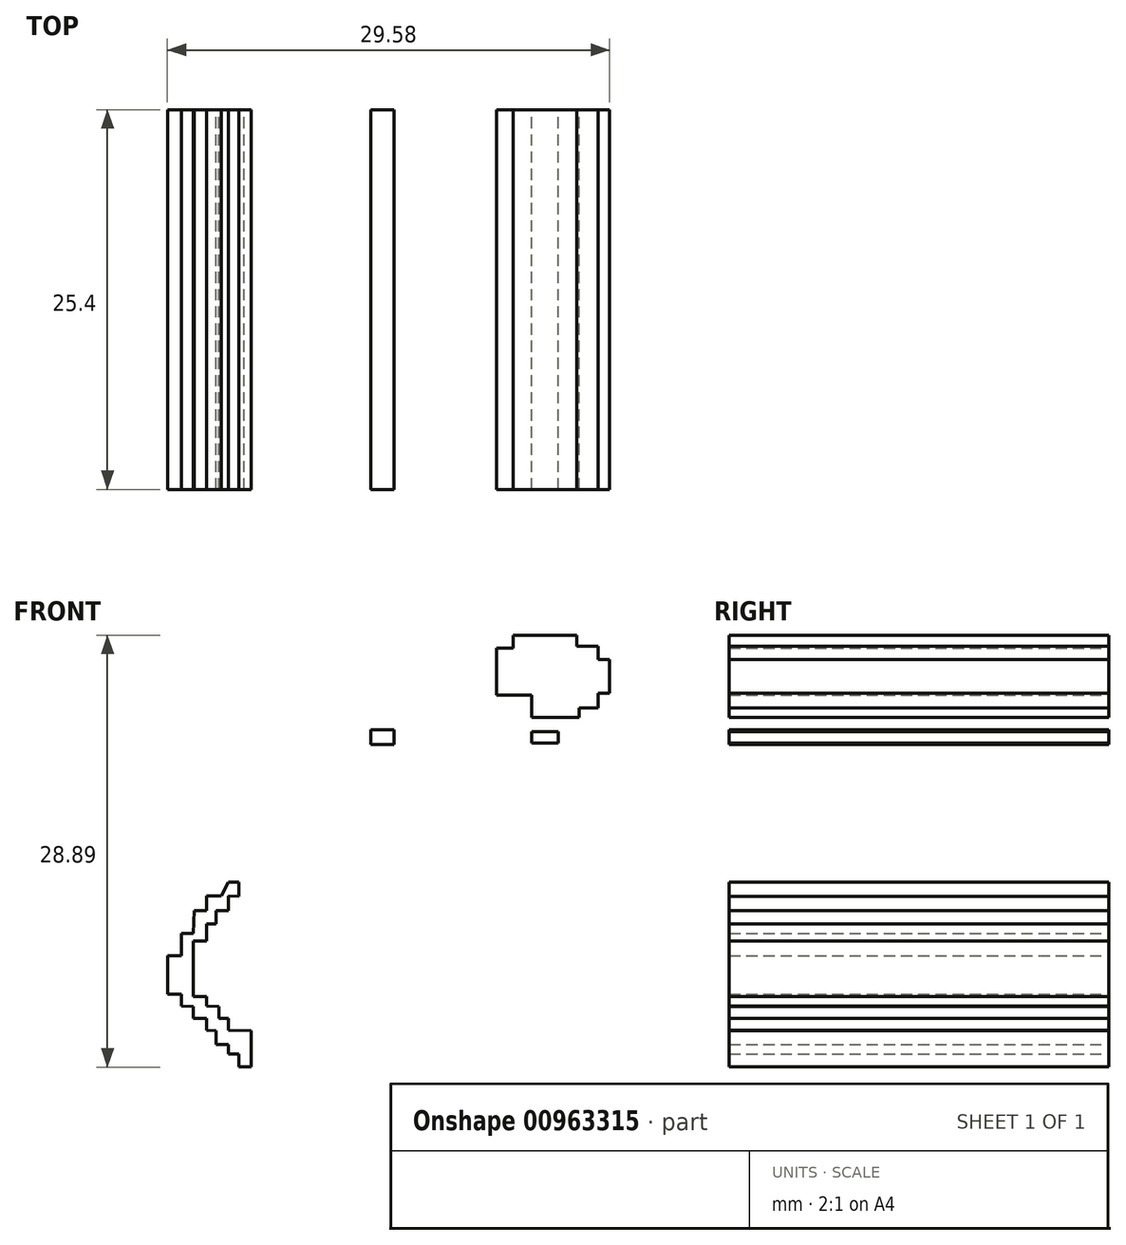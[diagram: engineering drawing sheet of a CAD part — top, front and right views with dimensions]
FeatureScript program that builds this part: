
annotation { "Feature Type Name" : "Feature", "Feature Type Description" : "" }
export const myFeature = defineFeature(function(context is Context, id is Id, definition is map)
    precondition{}
    {
        {
            var Q0;
            Q0=qCreatedBy(makeId("Front.planeOp"),FACE);
            var sketch = newSketch(context, id + "F0", { "sketchPlane" : qUnion([Q0])});
            skLineSegment(sketch, "E0", {"start": v(-16.56, -0.87) * mm, "end": v(-25.56, -0.87) * mm});
            skLineSegment(sketch, "E1", {"start": v(-25.56, -0.87) * mm, "end": v(-25.56, -1.62) * mm});
            skLineSegment(sketch, "E2", {"start": v(-25.56, -1.62) * mm, "end": v(-28.06, -1.62) * mm});
            skLineSegment(sketch, "E3", {"start": v(-28.06, -1.62) * mm, "end": v(-28.06, -2.38) * mm});
            skLineSegment(sketch, "E4", {"start": v(-28.06, -2.38) * mm, "end": v(-29.45, -2.38) * mm});
            skLineSegment(sketch, "E5", {"start": v(-29.45, -2.38) * mm, "end": v(-29.45, -3.02) * mm});
            skLineSegment(sketch, "E6", {"start": v(-29.45, -3.02) * mm, "end": v(-30.32, -3.02) * mm});
            skLineSegment(sketch, "E7", {"start": v(-30.32, -3.02) * mm, "end": v(-30.32, -4) * mm});
            skLineSegment(sketch, "E8", {"start": v(-30.32, -4) * mm, "end": v(-31.14, -4) * mm});
            skLineSegment(sketch, "E9", {"start": v(-31.14, -4) * mm, "end": v(-31.14, -4.59) * mm});
            skLineSegment(sketch, "E10", {"start": v(-31.14, -4.59) * mm, "end": v(-31.72, -4.59) * mm});
            skLineSegment(sketch, "E11", {"start": v(-31.72, -4.59) * mm, "end": v(-31.72, -5.46) * mm});
            skLineSegment(sketch, "E12", {"start": v(-31.72, -5.46) * mm, "end": v(-31.72, -6.27) * mm});
            skLineSegment(sketch, "E13", {"start": v(-31.72, -6.27) * mm, "end": v(-32.42, -6.27) * mm});
            skLineSegment(sketch, "E14", {"start": v(-32.42, -6.27) * mm, "end": v(-32.42, -11.56) * mm});
            skLineSegment(sketch, "E15", {"start": v(-32.42, -11.56) * mm, "end": v(-31.72, -11.56) * mm});
            skLineSegment(sketch, "E16", {"start": v(-31.72, -11.56) * mm, "end": v(-31.72, -13) * mm});
            skLineSegment(sketch, "E17", {"start": v(-31.72, -13) * mm, "end": v(-31.14, -13) * mm});
            skLineSegment(sketch, "E18", {"start": v(-31.14, -13) * mm, "end": v(-31.14, -14.11) * mm});
            skLineSegment(sketch, "E19", {"start": v(-31.14, -14.11) * mm, "end": v(-31.14, -14.64) * mm});
            skLineSegment(sketch, "E20", {"start": v(-31.14, -14.64) * mm, "end": v(-31.72, -14.64) * mm});
            skLineSegment(sketch, "E21", {"start": v(-31.72, -14.64) * mm, "end": v(-31.72, -15.74) * mm});
            skLineSegment(sketch, "E22", {"start": v(-31.72, -15.74) * mm, "end": v(-31.72, -17.42) * mm});
            skLineSegment(sketch, "E23", {"start": v(-31.72, -17.42) * mm, "end": v(-31.14, -17.42) * mm});
            skLineSegment(sketch, "E24", {"start": v(-31.14, -17.42) * mm, "end": v(-31.14, -18.53) * mm});
            skLineSegment(sketch, "E25", {"start": v(-31.14, -18.53) * mm, "end": v(-31.14, -19.22) * mm});
            skLineSegment(sketch, "E26", {"start": v(-31.14, -19.22) * mm, "end": v(-30.32, -19.22) * mm});
            skLineSegment(sketch, "E27", {"start": v(-30.32, -19.22) * mm, "end": v(-30.32, -19.75) * mm});
            skLineSegment(sketch, "E28", {"start": v(-30.32, -19.75) * mm, "end": v(-30.32, -20.39) * mm});
            skLineSegment(sketch, "E29", {"start": v(-30.32, -20.39) * mm, "end": v(-29.45, -20.39) * mm});
            skLineSegment(sketch, "E30", {"start": v(-29.45, -20.39) * mm, "end": v(-29.45, -20.9) * mm});
            skLineSegment(sketch, "E31", {"start": v(-29.45, -20.9) * mm, "end": v(-28.06, -20.9) * mm});
            skLineSegment(sketch, "E32", {"start": v(-28.06, -20.9) * mm, "end": v(-28.06, -21.55) * mm});
            skLineSegment(sketch, "E33", {"start": v(-28.06, -21.55) * mm, "end": v(-26.78, -21.55) * mm});
            skLineSegment(sketch, "E34", {"start": v(-26.78, -21.55) * mm, "end": v(-25.56, -21.55) * mm});
            skLineSegment(sketch, "E35", {"start": v(-25.56, -21.55) * mm, "end": v(-25.56, -22.19) * mm});
            skLineSegment(sketch, "E36", {"start": v(-25.56, -22.19) * mm, "end": v(-16.62, -22.19) * mm});
            skLineSegment(sketch, "E37", {"start": v(-16.62, -22.19) * mm, "end": v(-16.2, -21.55) * mm});
            skLineSegment(sketch, "E38", {"start": v(-16.2, -21.55) * mm, "end": v(-13.89, -21.55) * mm});
            skLineSegment(sketch, "E39", {"start": v(-13.89, -21.55) * mm, "end": v(-13.89, -20.56) * mm});
            skLineSegment(sketch, "E40", {"start": v(-13.89, -20.56) * mm, "end": v(-12.67, -20.56) * mm});
            skLineSegment(sketch, "E41", {"start": v(-12.67, -20.56) * mm, "end": v(-12.67, -19.75) * mm});
            skLineSegment(sketch, "E42", {"start": v(-12.67, -19.75) * mm, "end": v(-11.62, -19.75) * mm});
            skLineSegment(sketch, "E43", {"start": v(-11.62, -19.75) * mm, "end": v(-11.62, -19.05) * mm});
            skLineSegment(sketch, "E44", {"start": v(-11.62, -19.05) * mm, "end": v(-10.92, -19.05) * mm});
            skLineSegment(sketch, "E45", {"start": v(-10.92, -19.05) * mm, "end": v(-10.92, -17.77) * mm});
            skLineSegment(sketch, "E46", {"start": v(-10.92, -17.77) * mm, "end": v(-10.17, -17.77) * mm});
            skLineSegment(sketch, "E47", {"start": v(-10.17, -17.77) * mm, "end": v(-10.17, -14.87) * mm});
            skLineSegment(sketch, "E48", {"start": v(-10.17, -14.87) * mm, "end": v(-10.92, -14.87) * mm});
            skLineSegment(sketch, "E49", {"start": v(-10.92, -14.87) * mm, "end": v(-10.92, -13.07) * mm});
            skLineSegment(sketch, "E50", {"start": v(-10.92, -13.07) * mm, "end": v(-10.17, -13.07) * mm});
            skLineSegment(sketch, "E51", {"start": v(-10.17, -13.07) * mm, "end": v(-10.17, -11.73) * mm});
            skLineSegment(sketch, "E52", {"start": v(-10.17, -11.73) * mm, "end": v(-9.12, -11.73) * mm});
            skLineSegment(sketch, "E53", {"start": v(-9.12, -11.73) * mm, "end": v(-9.12, -6.44) * mm});
            skLineSegment(sketch, "E54", {"start": v(-9.12, -6.44) * mm, "end": v(-10.17, -6.44) * mm});
            skPoint(sketch, "E54.endSnap0", {"position": v(-10.17, -12.4) * mm});
            skLineSegment(sketch, "E55", {"start": v(-10.17, -6.44) * mm, "end": v(-10.17, -4.76) * mm});
            skLineSegment(sketch, "E56", {"start": v(-10.17, -4.76) * mm, "end": v(-10.92, -4.76) * mm});
            skLineSegment(sketch, "E57", {"start": v(-10.92, -4.76) * mm, "end": v(-10.92, -4.06) * mm});
            skLineSegment(sketch, "E58", {"start": v(-10.92, -4.06) * mm, "end": v(-11.62, -4.06) * mm});
            skLineSegment(sketch, "E59", {"start": v(-11.62, -4.06) * mm, "end": v(-11.62, -3.2) * mm});
            skLineSegment(sketch, "E60", {"start": v(-11.62, -3.2) * mm, "end": v(-12.67, -3.2) * mm});
            skLineSegment(sketch, "E61", {"start": v(-12.67, -3.2) * mm, "end": v(-12.67, -2.5) * mm});
            skLineSegment(sketch, "E62", {"start": v(-12.67, -2.5) * mm, "end": v(-13.89, -2.5) * mm});
            skLineSegment(sketch, "E63", {"start": v(-13.89, -2.5) * mm, "end": v(-13.89, -1.62) * mm});
            skLineSegment(sketch, "E64", {"start": v(-13.89, -1.62) * mm, "end": v(-16.2, -1.62) * mm});
            skLineSegment(sketch, "E65", {"start": v(-16.2, -1.62) * mm, "end": v(-16.2, -0.87) * mm});
            skLineSegment(sketch, "E66", {"start": v(-28.06, -7.55) * mm, "end": v(-24.17, -7.55) * mm});
            skLineSegment(sketch, "E67", {"start": v(-24.17, -8.42) * mm, "end": v(-23.24, -8.42) * mm});
            skLineSegment(sketch, "E68", {"start": v(-23.24, -8.42) * mm, "end": v(-23.24, -11.73) * mm});
            skLineSegment(sketch, "E69", {"start": v(-23.24, -11.73) * mm, "end": v(-24.17, -11.73) * mm});
            skLineSegment(sketch, "E70", {"start": v(-24.17, -11.73) * mm, "end": v(-24.17, -13.07) * mm});
            skLineSegment(sketch, "E71", {"start": v(-24.17, -13.07) * mm, "end": v(-24.8, -13.07) * mm});
            skLineSegment(sketch, "E72", {"start": v(-24.8, -13.07) * mm, "end": v(-24.8, -13.88) * mm});
            skLineSegment(sketch, "E73", {"start": v(-24.8, -13.88) * mm, "end": v(-25.56, -13.88) * mm});
            skLineSegment(sketch, "E74", {"start": v(-25.56, -13.88) * mm, "end": v(-25.56, -14.87) * mm});
            skLineSegment(sketch, "E75", {"start": v(-25.56, -14.87) * mm, "end": v(-27.13, -14.87) * mm});
            skLineSegment(sketch, "E76", {"start": v(-27.13, -14.87) * mm, "end": v(-27.13, -13.88) * mm});
            skLineSegment(sketch, "E77", {"start": v(-27.13, -13.88) * mm, "end": v(-25.56, -13.88) * mm});
            skLineSegment(sketch, "E78", {"start": v(-25.56, -13.88) * mm, "end": v(-25.56, -13.07) * mm});
            skLineSegment(sketch, "E79", {"start": v(-25.56, -13.07) * mm, "end": v(-27.13, -13.07) * mm});
            skLineSegment(sketch, "E80", {"start": v(-27.13, -13.07) * mm, "end": v(-28.06, -13.07) * mm});
            skLineSegment(sketch, "E81", {"start": v(-28.06, -13.07) * mm, "end": v(-28.76, -13.07) * mm});
            skLineSegment(sketch, "E82", {"start": v(-28.76, -13.07) * mm, "end": v(-28.76, -12.2) * mm});
            skLineSegment(sketch, "E83", {"start": v(-28.76, -12.2) * mm, "end": v(-29.92, -12.2) * mm});
            skLineSegment(sketch, "E84", {"start": v(-29.92, -12.2) * mm, "end": v(-29.92, -11.56) * mm});
            skLineSegment(sketch, "E85", {"start": v(-29.92, -11.56) * mm, "end": v(-30.73, -11.56) * mm});
            skLineSegment(sketch, "E86", {"start": v(-30.73, -11.56) * mm, "end": v(-30.73, -9.52) * mm});
            skLineSegment(sketch, "E87", {"start": v(-30.73, -9.52) * mm, "end": v(-29.92, -9.52) * mm});
            skLineSegment(sketch, "E88", {"start": v(-29.92, -9.52) * mm, "end": v(-29.92, -8.54) * mm});
            skLineSegment(sketch, "E89", {"start": v(-29.92, -8.54) * mm, "end": v(-28.93, -8.54) * mm});
            skLineSegment(sketch, "E90", {"start": v(-28.93, -8.54) * mm, "end": v(-28.93, -7.55) * mm});
            skLineSegment(sketch, "E91", {"start": v(-28.93, -7.55) * mm, "end": v(-28.06, -7.55) * mm});
            skLineSegment(sketch, "E92", {"start": v(-13.36, -7.55) * mm, "end": v(-17.6, -7.55) * mm});
            skLineSegment(sketch, "E93", {"start": v(-17.6, -7.55) * mm, "end": v(-17.6, -8.42) * mm});
            skLineSegment(sketch, "E94", {"start": v(-17.6, -8.42) * mm, "end": v(-18.7, -8.42) * mm});
            skLineSegment(sketch, "E95", {"start": v(-18.7, -8.42) * mm, "end": v(-18.7, -11.56) * mm});
            skLineSegment(sketch, "E96", {"start": v(-18.7, -11.56) * mm, "end": v(-17.6, -11.56) * mm});
            skLineSegment(sketch, "E97", {"start": v(-17.6, -11.56) * mm, "end": v(-17.6, -12.95) * mm});
            skLineSegment(sketch, "E98", {"start": v(-17.6, -12.95) * mm, "end": v(-16.85, -12.95) * mm});
            skLineSegment(sketch, "E99", {"start": v(-16.85, -12.95) * mm, "end": v(-16.85, -14) * mm});
            skLineSegment(sketch, "E100", {"start": v(-16.85, -14) * mm, "end": v(-16.38, -14) * mm});
            skLineSegment(sketch, "E101", {"start": v(-16.38, -14) * mm, "end": v(-14.58, -14) * mm});
            skLineSegment(sketch, "E102", {"start": v(-14.58, -14) * mm, "end": v(-14.58, -14.75) * mm});
            skLineSegment(sketch, "E103", {"start": v(-14.58, -14.75) * mm, "end": v(-16.38, -14.75) * mm});
            skLineSegment(sketch, "E104", {"start": v(-16.38, -14.75) * mm, "end": v(-16.38, -14) * mm});
            skLineSegment(sketch, "E105", {"start": v(-16.38, -13.07) * mm, "end": v(-13.19, -13.07) * mm});
            skLineSegment(sketch, "E106", {"start": v(-13.19, -13.07) * mm, "end": v(-13.19, -12.43) * mm});
            skLineSegment(sketch, "E107", {"start": v(-13.19, -12.43) * mm, "end": v(-11.91, -12.43) * mm});
            skLineSegment(sketch, "E108", {"start": v(-11.91, -12.43) * mm, "end": v(-11.91, -11.44) * mm});
            skLineSegment(sketch, "E109", {"start": v(-11.91, -11.44) * mm, "end": v(-11.16, -11.44) * mm});
            skLineSegment(sketch, "E110", {"start": v(-11.16, -11.44) * mm, "end": v(-11.16, -9.7) * mm});
            skLineSegment(sketch, "E111", {"start": v(-11.16, -9.7) * mm, "end": v(-11.16, -9.18) * mm});
            skLineSegment(sketch, "E112", {"start": v(-11.16, -9.18) * mm, "end": v(-11.91, -9.18) * mm});
            skLineSegment(sketch, "E113", {"start": v(-11.91, -9.18) * mm, "end": v(-11.91, -8.3) * mm});
            skLineSegment(sketch, "E114", {"start": v(-11.91, -8.3) * mm, "end": v(-13.36, -8.3) * mm});
            skLineSegment(sketch, "E115", {"start": v(-13.36, -8.3) * mm, "end": v(-13.36, -7.55) * mm});
            skLineSegment(sketch, "E116", {"start": v(-16.38, -8.3) * mm, "end": v(-14.12, -8.3) * mm});
            skLineSegment(sketch, "E117", {"start": v(-16.38, -8.3) * mm, "end": v(-16.38, -9.3) * mm});
            skLineSegment(sketch, "E118", {"start": v(-17.2, -9.3) * mm, "end": v(-17.2, -10.05) * mm});
            skLineSegment(sketch, "E119", {"start": v(-17.2, -10.05) * mm, "end": v(-18.13, -10.05) * mm});
            skLineSegment(sketch, "E120", {"start": v(-18.13, -10.05) * mm, "end": v(-18.13, -10.63) * mm});
            skLineSegment(sketch, "E121", {"start": v(-18.13, -10.63) * mm, "end": v(-17.6, -10.63) * mm});
            skLineSegment(sketch, "E122", {"start": v(-17.6, -10.63) * mm, "end": v(-17.6, -11.56) * mm});
            skLineSegment(sketch, "E123", {"start": v(-17.6, -11.56) * mm, "end": v(-17.2, -11.56) * mm});
            skLineSegment(sketch, "E124", {"start": v(-17.2, -11.56) * mm, "end": v(-16.38, -11.56) * mm});
            skLineSegment(sketch, "E125", {"start": v(-16.38, -11.56) * mm, "end": v(-16.38, -13.07) * mm});
            skLineSegment(sketch, "E126", {"start": v(-16.38, -12.4) * mm, "end": v(-14.06, -12.4) * mm});
            skPoint(sketch, "E126.startSnap0", {"position": v(-24.17, -12.4) * mm});
            skLineSegment(sketch, "E127", {"start": v(-14.06, -12.4) * mm, "end": v(-14.06, -11.61) * mm});
            skLineSegment(sketch, "E128", {"start": v(-14.06, -11.61) * mm, "end": v(-13.19, -11.61) * mm});
            skLineSegment(sketch, "E129", {"start": v(-13.19, -11.61) * mm, "end": v(-13.19, -10.74) * mm});
            skLineSegment(sketch, "E130", {"start": v(-13.19, -10.74) * mm, "end": v(-12.55, -10.74) * mm});
            skLineSegment(sketch, "E131", {"start": v(-12.55, -10.74) * mm, "end": v(-12.55, -10.05) * mm});
            skLineSegment(sketch, "E132", {"start": v(-12.55, -10.05) * mm, "end": v(-13.19, -10.05) * mm});
            skLineSegment(sketch, "E133", {"start": v(-13.19, -10.05) * mm, "end": v(-13.19, -9.3) * mm});
            skLineSegment(sketch, "E134", {"start": v(-13.19, -9.3) * mm, "end": v(-14.12, -9.3) * mm});
            skLineSegment(sketch, "E135", {"start": v(-14.12, -9.3) * mm, "end": v(-14.12, -8.3) * mm});
            skLineSegment(sketch, "E136", {"start": v(-17.2, -9.3) * mm, "end": v(-16.38, -9.3) * mm});
            skLineSegment(sketch, "E137", {"start": v(-21.51, -11.63) * mm, "end": v(-21.51, -13.07) * mm});
            skLineSegment(sketch, "E138", {"start": v(-21.51, -13.07) * mm, "end": v(-22.3, -13.07) * mm});
            skLineSegment(sketch, "E139", {"start": v(-22.3, -13.07) * mm, "end": v(-22.3, -15.29) * mm});
            skLineSegment(sketch, "E140", {"start": v(-22.3, -15.29) * mm, "end": v(-19.13, -15.29) * mm});
            skLineSegment(sketch, "E141", {"start": v(-19.13, -15.29) * mm, "end": v(-19.13, -13.07) * mm});
            skLineSegment(sketch, "E142", {"start": v(-19.13, -13.07) * mm, "end": v(-19.95, -13.07) * mm});
            skLineSegment(sketch, "E143", {"start": v(-19.95, -13.07) * mm, "end": v(-19.95, -11.51) * mm});
            skLineSegment(sketch, "E144", {"start": v(-19.95, -11.51) * mm, "end": v(-21.51, -11.51) * mm});
            skLineSegment(sketch, "E145", {"start": v(-28.37, -14.87) * mm, "end": v(-28.37, -15.95) * mm});
            skLineSegment(sketch, "E146", {"start": v(-28.37, -15.95) * mm, "end": v(-29.93, -15.95) * mm});
            skLineSegment(sketch, "E147", {"start": v(-29.93, -16.27) * mm, "end": v(-29.93, -17.01) * mm});
            skLineSegment(sketch, "E148", {"start": v(-29.93, -17.01) * mm, "end": v(-28.37, -17.01) * mm});
            skLineSegment(sketch, "E149", {"start": v(-28.37, -14.87) * mm, "end": v(-28.37, -14.43) * mm});
            skLineSegment(sketch, "E150", {"start": v(-28.37, -14.43) * mm, "end": v(-27.71, -14.43) * mm});
            skLineSegment(sketch, "E151", {"start": v(-27.71, -14.43) * mm, "end": v(-27.71, -15.17) * mm});
            skLineSegment(sketch, "E152", {"start": v(-27.71, -15.17) * mm, "end": v(-27.13, -15.17) * mm});
            skLineSegment(sketch, "E153", {"start": v(-27.13, -15.17) * mm, "end": v(-26.77, -15.17) * mm});
            skLineSegment(sketch, "E154", {"start": v(-26.77, -15.17) * mm, "end": v(-26.77, -15.95) * mm});
            skLineSegment(sketch, "E155", {"start": v(-26.77, -15.95) * mm, "end": v(-25.5, -15.95) * mm});
            skLineSegment(sketch, "E156", {"start": v(-25.5, -15.95) * mm, "end": v(-25.5, -16.64) * mm});
            skLineSegment(sketch, "E157", {"start": v(-25.5, -16.64) * mm, "end": v(-15.6, -16.64) * mm});
            skLineSegment(sketch, "E158", {"start": v(-15.6, -16.64) * mm, "end": v(-15.31, -15.95) * mm});
            skLineSegment(sketch, "E159", {"start": v(-15.31, -15.95) * mm, "end": v(-14.12, -15.95) * mm});
            skLineSegment(sketch, "E160", {"start": v(-14.12, -15.95) * mm, "end": v(-14.12, -14.87) * mm});
            skLineSegment(sketch, "E161", {"start": v(-14.12, -14.87) * mm, "end": v(-14.12, -14.43) * mm});
            skLineSegment(sketch, "E162", {"start": v(-14.12, -14.43) * mm, "end": v(-13.19, -14.43) * mm});
            skLineSegment(sketch, "E163", {"start": v(-13.19, -14.43) * mm, "end": v(-13.19, -15.17) * mm});
            skLineSegment(sketch, "E164", {"start": v(-13.19, -15.17) * mm, "end": v(-12.35, -15.17) * mm});
            skLineSegment(sketch, "E165", {"start": v(-12.35, -15.17) * mm, "end": v(-12.35, -15.95) * mm});
            skLineSegment(sketch, "E166", {"start": v(-12.35, -15.95) * mm, "end": v(-11.37, -15.95) * mm});
            skLineSegment(sketch, "E167", {"start": v(-11.37, -15.95) * mm, "end": v(-11.37, -16.64) * mm});
            skLineSegment(sketch, "E168", {"start": v(-11.37, -16.64) * mm, "end": v(-12.8, -16.64) * mm});
            skLineSegment(sketch, "E169", {"start": v(-12.8, -16.64) * mm, "end": v(-12.8, -17.5) * mm});
            skLineSegment(sketch, "E170", {"start": v(-12.8, -17.5) * mm, "end": v(-13.83, -17.5) * mm});
            skLineSegment(sketch, "E171", {"start": v(-13.83, -17.5) * mm, "end": v(-13.83, -18.2) * mm});
            skLineSegment(sketch, "E172", {"start": v(-13.83, -18.2) * mm, "end": v(-14.49, -18.2) * mm});
            skLineSegment(sketch, "E173", {"start": v(-14.49, -18.2) * mm, "end": v(-14.49, -18.9) * mm});
            skLineSegment(sketch, "E174", {"start": v(-14.49, -18.9) * mm, "end": v(-15.31, -18.9) * mm});
            skLineSegment(sketch, "E175", {"start": v(-15.31, -18.9) * mm, "end": v(-15.31, -19.75) * mm});
            skLineSegment(sketch, "E176", {"start": v(-15.31, -19.75) * mm, "end": v(-16.38, -19.75) * mm});
            skLineSegment(sketch, "E177", {"start": v(-16.38, -19.75) * mm, "end": v(-17, -19.75) * mm});
            skLineSegment(sketch, "E178", {"start": v(-17, -19.75) * mm, "end": v(-17, -20.39) * mm});
            skLineSegment(sketch, "E179", {"start": v(-17, -20.39) * mm, "end": v(-23.57, -20.39) * mm});
            skLineSegment(sketch, "E180", {"start": v(-23.57, -20.39) * mm, "end": v(-23.57, -19.64) * mm});
            skLineSegment(sketch, "E181", {"start": v(-23.94, -19.73) * mm, "end": v(-25.3, -19.73) * mm});
            skLineSegment(sketch, "E182", {"start": v(-25.3, -19.73) * mm, "end": v(-25.3, -19.1) * mm});
            skLineSegment(sketch, "E183", {"start": v(-25.3, -19.1) * mm, "end": v(-26.77, -19.1) * mm});
            skLineSegment(sketch, "E184", {"start": v(-26.77, -19.1) * mm, "end": v(-26.77, -18.33) * mm});
            skLineSegment(sketch, "E185", {"start": v(-26.77, -18.33) * mm, "end": v(-27.47, -18.33) * mm});
            skLineSegment(sketch, "E186", {"start": v(-27.47, -18.33) * mm, "end": v(-27.47, -17.71) * mm});
            skLineSegment(sketch, "E187", {"start": v(-27.47, -17.71) * mm, "end": v(-27.92, -17.71) * mm});
            skLineSegment(sketch, "E188", {"start": v(-27.92, -17.71) * mm, "end": v(-28.37, -17.71) * mm});
            skLineSegment(sketch, "E189", {"start": v(-28.37, -17.71) * mm, "end": v(-28.37, -17.01) * mm});
            skLineSegment(sketch, "E190", {"start": v(-32.22, -19.41) * mm, "end": v(-34.35, -19.41) * mm});
            skLineSegment(sketch, "E191", {"start": v(-34.35, -19.41) * mm, "end": v(-34.35, -20.14) * mm});
            skLineSegment(sketch, "E192", {"start": v(-34.18, -20.14) * mm, "end": v(-35.16, -20.14) * mm});
            skLineSegment(sketch, "E193", {"start": v(-35.18, -20.2) * mm, "end": v(-35.18, -21.55) * mm});
            skLineSegment(sketch, "E194", {"start": v(-35.3, -21.6) * mm, "end": v(-36.08, -21.6) * mm});
            skLineSegment(sketch, "E195", {"start": v(-36.08, -21.6) * mm, "end": v(-36.08, -22.7) * mm});
            skLineSegment(sketch, "E196", {"start": v(-36.16, -22.7) * mm, "end": v(-35.13, -22.7) * mm});
            skLineSegment(sketch, "E197", {"start": v(-35.13, -22.7) * mm, "end": v(-35.13, -21.93) * mm});
            skLineSegment(sketch, "E198", {"start": v(-35.13, -21.93) * mm, "end": v(-33.18, -21.93) * mm});
            skLineSegment(sketch, "E199", {"start": v(-33.18, -21.93) * mm, "end": v(-33.18, -22.7) * mm});
            skLineSegment(sketch, "E200", {"start": v(-33.18, -22.7) * mm, "end": v(-30.73, -22.7) * mm});
            skLineSegment(sketch, "E201", {"start": v(-30.73, -22.7) * mm, "end": v(-30.73, -23.4) * mm});
            skLineSegment(sketch, "E202", {"start": v(-30.73, -23.4) * mm, "end": v(-29.93, -23.4) * mm});
            skLineSegment(sketch, "E203", {"start": v(-29.93, -23.4) * mm, "end": v(-29.93, -24.17) * mm});
            skLineSegment(sketch, "E204", {"start": v(-29.86, -24.2) * mm, "end": v(-28.46, -24.2) * mm});
            skLineSegment(sketch, "E205", {"start": v(-28.34, -24.25) * mm, "end": v(-28.34, -24.98) * mm});
            skLineSegment(sketch, "E206", {"start": v(-28.37, -25) * mm, "end": v(-27.7, -25) * mm});
            skLineSegment(sketch, "E207", {"start": v(-27.7, -25) * mm, "end": v(-27.7, -28.52) * mm});
            skLineSegment(sketch, "E208", {"start": v(-27.7, -28.52) * mm, "end": v(-30.56, -28.52) * mm});
            skLineSegment(sketch, "E209", {"start": v(-30.56, -28.52) * mm, "end": v(-30.56, -29.25) * mm});
            skLineSegment(sketch, "E210", {"start": v(-30.56, -29.25) * mm, "end": v(-31.22, -29.25) * mm});
            skLineSegment(sketch, "E211", {"start": v(-31.22, -29.25) * mm, "end": v(-31.22, -28.52) * mm});
            skLineSegment(sketch, "E212", {"start": v(-31.22, -28.57) * mm, "end": v(-31.9, -28.52) * mm});
            skLineSegment(sketch, "E213", {"start": v(-31.93, -28.5) * mm, "end": v(-31.9, -25) * mm});
            skLineSegment(sketch, "E214", {"start": v(-31.9, -25) * mm, "end": v(-31.9, -24.76) * mm});
            skLineSegment(sketch, "E215", {"start": v(-31.9, -24.76) * mm, "end": v(-32.81, -24.76) * mm});
            skLineSegment(sketch, "E216", {"start": v(-32.81, -24.76) * mm, "end": v(-33.13, -24.76) * mm});
            skLineSegment(sketch, "E217", {"start": v(-33.13, -24.76) * mm, "end": v(-33.13, -29.57) * mm});
            skLineSegment(sketch, "E218", {"start": v(-33.13, -29.57) * mm, "end": v(-33.13, -30.75) * mm});
            skLineSegment(sketch, "E219", {"start": v(-33.13, -30.75) * mm, "end": v(-33.77, -30.74) * mm});
            skLineSegment(sketch, "E220", {"start": v(-33.77, -30.74) * mm, "end": v(-33.77, -36.44) * mm});
            skLineSegment(sketch, "E221", {"start": v(-33.77, -36.44) * mm, "end": v(-34.52, -36.43) * mm});
            skLineSegment(sketch, "E222", {"start": v(-34.52, -36.43) * mm, "end": v(-35.13, -36.43) * mm});
            skLineSegment(sketch, "E223", {"start": v(-35.13, -36.43) * mm, "end": v(-35.13, -34) * mm});
            skLineSegment(sketch, "E224", {"start": v(-35.13, -34) * mm, "end": v(-36.67, -33.99) * mm});
            skLineSegment(sketch, "E225", {"start": v(-36.67, -33.99) * mm, "end": v(-36.67, -33.19) * mm});
            skLineSegment(sketch, "E226", {"start": v(-36.67, -33.19) * mm, "end": v(-37.3, -33.18) * mm});
            skLineSegment(sketch, "E227", {"start": v(-37.3, -33.18) * mm, "end": v(-37.3, -32.37) * mm});
            skLineSegment(sketch, "E228", {"start": v(-37.3, -32.37) * mm, "end": v(-38.12, -32.37) * mm});
            skLineSegment(sketch, "E229", {"start": v(-38.12, -32.37) * mm, "end": v(-38.12, -31.73) * mm});
            skLineSegment(sketch, "E230", {"start": v(-38.12, -31.73) * mm, "end": v(-39, -31.73) * mm});
            skLineSegment(sketch, "E231", {"start": v(-39, -31.73) * mm, "end": v(-39, -28.52) * mm});
            skLineSegment(sketch, "E232", {"start": v(-39, -28.52) * mm, "end": v(-39, -28.02) * mm});
            skLineSegment(sketch, "E233", {"start": v(-39, -28.02) * mm, "end": v(-38.12, -28.02) * mm});
            skLineSegment(sketch, "E234", {"start": v(-38.12, -28.02) * mm, "end": v(-38.12, -26.85) * mm});
            skLineSegment(sketch, "E235", {"start": v(-38.12, -26.85) * mm, "end": v(-37.48, -26.86) * mm});
            skLineSegment(sketch, "E236", {"start": v(-37.48, -26.86) * mm, "end": v(-37.48, -25.98) * mm});
            skLineSegment(sketch, "E237", {"start": v(-37.48, -25.98) * mm, "end": v(-36.67, -25.99) * mm});
            skLineSegment(sketch, "E238", {"start": v(-36.67, -25.99) * mm, "end": v(-36.67, -25) * mm});
            skLineSegment(sketch, "E239", {"start": v(-36.67, -25) * mm, "end": v(-35.97, -25) * mm});
            skLineSegment(sketch, "E240", {"start": v(-35.97, -25) * mm, "end": v(-35.97, -24.07) * mm});
            skLineSegment(sketch, "E241", {"start": v(-35.97, -24.07) * mm, "end": v(-36.67, -24.06) * mm});
            skLineSegment(sketch, "E242", {"start": v(-36.67, -24.06) * mm, "end": v(-37.13, -25) * mm});
            skLineSegment(sketch, "E243", {"start": v(-37.13, -25) * mm, "end": v(-38.12, -25) * mm});
            skLineSegment(sketch, "E244", {"start": v(-38.12, -25) * mm, "end": v(-38.12, -25.99) * mm});
            skLineSegment(sketch, "E245", {"start": v(-38.12, -25.99) * mm, "end": v(-38.12, -26.85) * mm});
            skLineSegment(sketch, "E246", {"start": v(-38.12, -25.99) * mm, "end": v(-38.94, -25.98) * mm});
            skLineSegment(sketch, "E247", {"start": v(-38.94, -25.98) * mm, "end": v(-39, -27.5) * mm});
            skLineSegment(sketch, "E248", {"start": v(-39, -27.5) * mm, "end": v(-39.8, -27.49) * mm});
            skLineSegment(sketch, "E249", {"start": v(-39.8, -27.49) * mm, "end": v(-39.8, -29) * mm});
            skLineSegment(sketch, "E250", {"start": v(-39.8, -29) * mm, "end": v(-40.74, -29) * mm});
            skLineSegment(sketch, "E251", {"start": v(-40.74, -29) * mm, "end": v(-40.74, -31.56) * mm});
            skLineSegment(sketch, "E252", {"start": v(-40.74, -31.56) * mm, "end": v(-39.8, -31.57) * mm});
            skLineSegment(sketch, "E253", {"start": v(-39.8, -31.57) * mm, "end": v(-39.8, -32.37) * mm});
            skLineSegment(sketch, "E254", {"start": v(-39.8, -32.37) * mm, "end": v(-39, -32.37) * mm});
            skLineSegment(sketch, "E255", {"start": v(-39, -32.37) * mm, "end": v(-39, -33.19) * mm});
            skLineSegment(sketch, "E256", {"start": v(-39, -33.19) * mm, "end": v(-38.12, -33.2) * mm});
            skLineSegment(sketch, "E257", {"start": v(-38.12, -33.2) * mm, "end": v(-38.12, -33.99) * mm});
            skLineSegment(sketch, "E258", {"start": v(-38.12, -33.99) * mm, "end": v(-37.48, -34) * mm});
            skLineSegment(sketch, "E259", {"start": v(-37.48, -34) * mm, "end": v(-37.48, -34.93) * mm});
            skLineSegment(sketch, "E260", {"start": v(-37.48, -34.93) * mm, "end": v(-36.67, -34.93) * mm});
            skLineSegment(sketch, "E261", {"start": v(-36.67, -34.93) * mm, "end": v(-36.67, -35.57) * mm});
            skLineSegment(sketch, "E262", {"start": v(-36.67, -35.57) * mm, "end": v(-35.97, -35.57) * mm});
            skLineSegment(sketch, "E263", {"start": v(-35.97, -35.57) * mm, "end": v(-35.97, -36.43) * mm});
            skLineSegment(sketch, "E264", {"start": v(-35.97, -36.43) * mm, "end": v(-35.6, -36.44) * mm});
            skPoint(sketch, "E264.endSnap0", {"position": v(-34.14, -36.44) * mm});
            skLineSegment(sketch, "E265", {"start": v(-35.6, -36.44) * mm, "end": v(-35.13, -36.43) * mm});
            skLineSegment(sketch, "E266", {"start": v(-34.52, -37.16) * mm, "end": v(-33.13, -37.17) * mm});
            skLineSegment(sketch, "E267", {"start": v(-33.13, -37.17) * mm, "end": v(-33.13, -37.86) * mm});
            skLineSegment(sketch, "E268", {"start": v(-33.13, -37.86) * mm, "end": v(-26.13, -37.9) * mm});
            skLineSegment(sketch, "E269", {"start": v(-26.13, -37.9) * mm, "end": v(-25.78, -37.9) * mm});
            skLineSegment(sketch, "E270", {"start": v(-25.78, -37.9) * mm, "end": v(-25.78, -37.22) * mm});
            skLineSegment(sketch, "E271", {"start": v(-25.78, -37.22) * mm, "end": v(-22.3, -37.24) * mm});
            skLineSegment(sketch, "E272", {"start": v(-22.3, -37.24) * mm, "end": v(-21.8, -37.25) * mm});
            skLineSegment(sketch, "E273", {"start": v(-21.8, -37.25) * mm, "end": v(-21.8, -36.43) * mm});
            skLineSegment(sketch, "E274", {"start": v(-21.8, -36.43) * mm, "end": v(-17.88, -36.46) * mm});
            skLineSegment(sketch, "E275", {"start": v(-17.88, -36.46) * mm, "end": v(-17.88, -37.16) * mm});
            skLineSegment(sketch, "E276", {"start": v(-17.88, -37.16) * mm, "end": v(-10.2, -37.21) * mm});
            skLineSegment(sketch, "E277", {"start": v(-10.2, -37.21) * mm, "end": v(-10.2, -37.82) * mm});
            skLineSegment(sketch, "E278", {"start": v(-10.2, -37.82) * mm, "end": v(-10.2, -38.08) * mm});
            skLineSegment(sketch, "E279", {"start": v(-10.2, -38.08) * mm, "end": v(-8.41, -38.1) * mm});
            skLineSegment(sketch, "E280", {"start": v(-8.41, -38.1) * mm, "end": v(-8.4, -36.55) * mm});
            skLineSegment(sketch, "E281", {"start": v(-8.4, -36.54) * mm, "end": v(-7.64, -36.55) * mm});
            skSolve(sketch);
        }
        {
            var Q0;
            Q0 = qSketchRegion(id + "F0", true);
            extrude(context, id + "F1", {"entities" : qUnion([Q0]), "depth" : 25.4 * mm, "offsetDistance" : 25.4 * mm});
        }
    });
